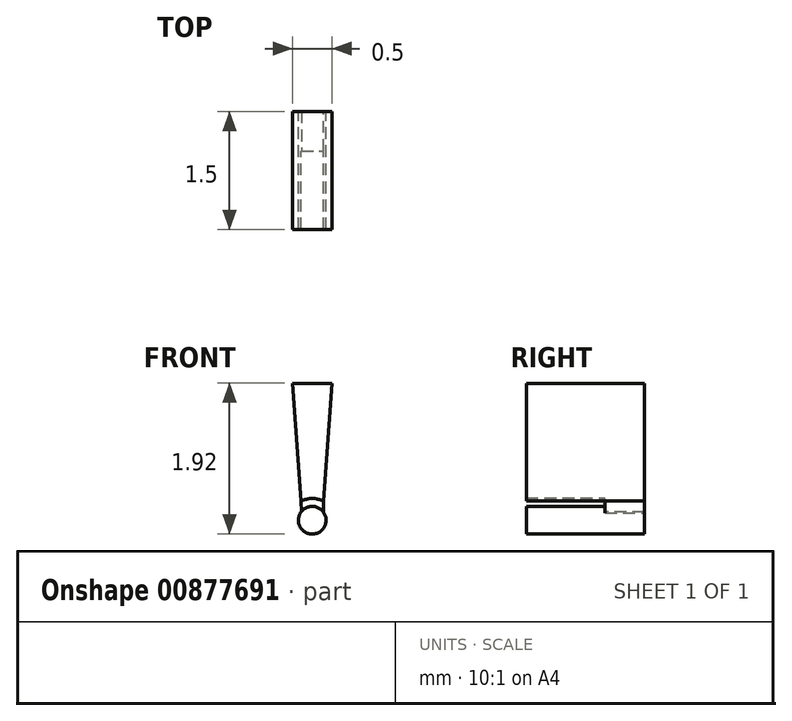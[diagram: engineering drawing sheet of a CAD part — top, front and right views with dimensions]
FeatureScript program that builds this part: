
annotation { "Feature Type Name" : "Feature", "Feature Type Description" : "" }
export const myFeature = defineFeature(function(context is Context, id is Id, definition is map)
    precondition{}
    {
        {
            var Q0;
            Q0=qCreatedBy(makeId("Front.planeOp"),FACE);
            var sketch = newSketch(context, id + "F0", { "sketchPlane" : qUnion([Q0])});
            skPoint(sketch, "E0.end.orphan", {"position": v(0, 0.4) * mm});
            skPoint(sketch, "E0.start.orphan", {"position": v(0, 0.8) * mm});
            skLineSegment(sketch, "E1", {"start": v(0, 2.63) * mm, "end": v(-0.25, 2.63) * mm});
            skLineSegment(sketch, "E2", {"start": v(-0.25, 2.63) * mm, "end": v(-0.15, 1.13) * mm});
            skLineSegment(sketch, "E3.MirrorCS", {"start": v(0, 2.63) * mm, "end": v(0.25, 2.63) * mm});
            skLineSegment(sketch, "E4.MirrorCS", {"start": v(0.25, 2.63) * mm, "end": v(0.15, 1.13) * mm});
            skFitSpline(sketch, "E5", {"points": [v(-0.15, 1.13) * mm, v(0, 1.17) * mm, v(0.15, 1.13) * mm], "startDerivative": vector(0.5, 0.16) * mm, "endDerivative": vector(0.5, -0.16) * mm});
            skLineSegment(sketch, "E6", {"start": v(0, 0.8) * mm, "end": v(0, 0.56) * mm});
            skPoint(sketch, "E7.MirrorCS.end.orphan", {"position": v(0, 0.56) * mm});
            skCircle(sketch, "E8", {"center": v(0, 0.89) * mm, "radius": 0.18 * mm});
            skSolve(sketch);
        }
        {
            var Q0;
            Q0=makeQuery(id+"F0.imprint","IMPRINT",FACE,{"disambiguationData":[TD([[makeQuery(id+"F0.imprint","IMPRINT",EDGE,{"derivedFrom":sQuery(id+"F0.wireOp",EDGE,"E1")}),1.0]])]});
            var Q1;
            Q1=makeQuery(id+"F0.imprint","IMPRINT",FACE,{"disambiguationData":[TD([[makeQuery(id+"F0.imprint","IMPRINT",EDGE,{"derivedFrom":sQuery(id+"F0.wireOp",EDGE,"E8")}),1.0]])]});
            extrude(context, id + "F1", {"entities" : qUnion([Q0, Q1]), "depth" : 1.5 * mm, "offsetDistance" : 25 * mm});
        }
        {
            var Q0;
            Q0=makeQuery(id+"F1.opExtrude","CAP_FACE",FACE,{"disambiguationData":[OSD([sQuery(id+"F0.wireOp",EDGE,"E1"),sQuery(id+"F0.wireOp",EDGE,"E2"),sQuery(id+"F0.wireOp",EDGE,"E3.MirrorCS"),sQuery(id+"F0.wireOp",EDGE,"E4.MirrorCS"),sQuery(id+"F0.wireOp",EDGE,"E5")])],"isStart":true});
            var sketch = newSketch(context, id + "F2", { "sketchPlane" : qUnion([Q0])});
            skLineSegment(sketch, "E9", {"start": v(-0.15, 1.13) * mm, "end": v(-0.15, 0.98) * mm});
            skLineSegment(sketch, "E10", {"start": v(0.15, 1.13) * mm, "end": v(0.14, 1) * mm});
            skFitSpline(sketch, "E11", {"points": [v(-0.15, 1.13) * mm, v(0, 1.17) * mm, v(0.15, 1.13) * mm], "startDerivative": vector(0.3, 0.1) * mm, "endDerivative": vector(0.3, -0.1) * mm});
            skArc(sketch, "E12", {"start": v(0.14, 1) * mm, "mid": v(0, 1.06) * mm, "end": v(-0.15, 0.98) * mm});
            skSolve(sketch);
        }
        {
            var Q0;
            {var subQ4=sQuery(id+"F2.wireOp",EDGE,"E9");Q0=makeQuery(id+"F2.imprint","IMPRINT",FACE,{"disambiguationData":[TD([[makeQuery(id+"F2.imprint","IMPRINT",EDGE,{"derivedFrom":subQ4}),1.0]])]});}
            extrude(context, id + "F3", {"entities" : qUnion([Q0]), "operationType" : NewBodyOperationType.ADD, "oppositeDirection" : true, "depth" : .5 * mm, "offsetDistance" : 25 * mm});
        }
    });
